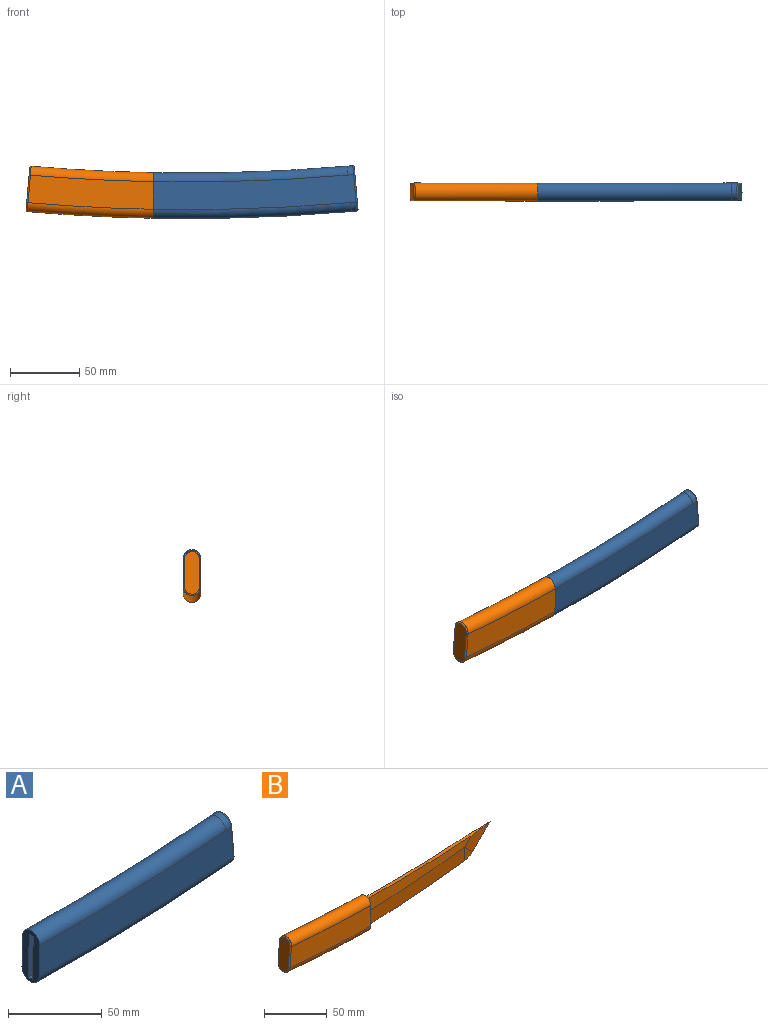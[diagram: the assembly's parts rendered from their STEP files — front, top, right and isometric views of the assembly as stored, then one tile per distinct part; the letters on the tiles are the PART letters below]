
ASSEMBLY  parts=2 mates=1
PART A: 17 faces, bbox 148.5x14.1x40.8 mm
  f0: cylinder r=1328mm len=140.41mm, axis (0,1,0), area 421.7mm2, adj f1,f3,f5,f8
  f1: plane 23.3x23.29mm, normal (-0.71,0,0.71), area 98.8mm2, adj f0,f2,f5,f8
  f2: cylinder r=1349.91mm len=117.63mm, axis (0,1,0), area 354.2mm2, adj f1,f3,f5,f8
  f3: plane 32.99x13mm, normal (-1,0,0.02), area 308.7mm2, adj f0,f2,f5,f6,f7,f8,f9,f11
  f4: plane 30.88x11mm, normal (1,0,0.09), area 315mm2, adj f13,f14,f15,f16
  f5: plane 140.94x32.77mm, normal (0,-1,0), area 3150.7mm2, adj f0,f1,f2,f3
  f6: plane 146.88x25.37mm, normal (0,1,0), area 2919.7mm2, adj f3,f9,f10,f11,f12,f14
  f7: plane 146.88x25.37mm, normal (0,-1,0), area 2919.7mm2, adj f3,f9,f10,f11,f12,f15
  f8: plane 140.94x32.77mm, normal (0,1,0), area 3150.7mm2, adj f0,f1,f2,f3
  f9: torus R=1351.5mm, axis (0,-1,0), area 2929.9mm2, adj f3,f6,f7,f10
  f10: cylinder r=6.5mm len=13mm, axis (1,0,0.09), area 81.7mm2, adj f6,f7,f9,f13
  f11: torus R=1331.5mm, axis (0,-1,0), area 2868.8mm2, adj f3,f6,f7,f12
  f12: cylinder r=6.5mm len=13mm, axis (-1,0,-0.09), area 81.7mm2, adj f6,f7,f11,f16
  f13: torus R=5.5mm, axis (1,0,0.09), area 30.3mm2, adj f4,f10,f14,f15
  f14: cylinder r=1mm len=20.01mm, axis (-0.09,0,1), area 31.4mm2, adj f4,f6,f13,f16
  f15: cylinder r=1mm len=20.01mm, axis (0.09,0,-1), area 31.4mm2, adj f4,f7,f13,f16
  f16: torus R=5.5mm, axis (1,0,0.09), area 30.3mm2, adj f4,f12,f14,f15
PART B: 19 faces, bbox 233.1x13x38.5 mm
  f0: plane 117.63x15.94mm, normal (0,1,0), area 1111.5mm2, adj f2,f4,f8,f12
  f1: plane 30.89x11mm, normal (-1,0,0.09), area 315mm2, adj f15,f16,f17,f18
  f2: plane 33x13mm, normal (1,0,-0.02), area 331.3mm2, adj f0,f3,f4,f5,f6,f7,f8,f13
  f3: plane 91.09x24.7mm, normal (0,-1,0), area 1803.5mm2, adj f2,f13,f14,f17
  f4: cylinder r=1328mm len=140.41mm, axis (0,1,0), area 387mm2, adj f0,f2,f5,f10,f12
  f5: plane 117.63x15.94mm, normal (0,-1,0), area 1111.5mm2, adj f2,f4,f7,f10
  f6: plane 91.09x24.7mm, normal (0,1,0), area 1803.5mm2, adj f2,f13,f14,f16
  f7: cone r=1334.91mm half-angle=84.3deg, axis (0,1,0), area 1685.6mm2, adj f2,f5,f8,f9
  f8: cone r=1349.91mm half-angle=84.3deg, axis (0,-1,0), area 1685.6mm2, adj f0,f2,f7,f11
  f9: cone r=15mm half-angle=84.3deg, axis (0,1,0), area 75.2mm2, adj f7,f10,f11
  f10: plane 30.26x19.65mm, normal (0.07,-1,-0.07), area 285.7mm2, adj f4,f5,f9,f12
  f11: cone r=15mm half-angle=84.3deg, axis (0,-1,0), area 75.2mm2, adj f8,f9,f12
  f12: plane 30.26x19.65mm, normal (0.07,1,-0.07), area 285.7mm2, adj f0,f4,f10,f11
  f13: torus R=1331.5mm, axis (0,-1,0), area 1821.8mm2, adj f2,f3,f6,f15
  f14: torus R=1351.5mm, axis (0,-1,0), area 1861mm2, adj f2,f3,f6,f18
  f15: bspline ~13x8.02mm, area 30.3mm2, adj f1,f13,f16,f17
  f16: cylinder r=1mm len=20.01mm, axis (-0.09,0,-1), area 31.4mm2, adj f1,f6,f15,f18
  f17: cylinder r=1mm len=20.01mm, axis (0.09,0,1), area 31.4mm2, adj f1,f3,f15,f18
  f18: bspline ~13x8.02mm, area 30.3mm2, adj f1,f14,f16,f17
PLACE A rot(axis=(0,1,0),0deg) t=(292.55,34.69,-102.62)mm fixed
PLACE B rot(axis=(0,-1,0),0deg) t=(-97.55,34.69,-15.68)mm
MATE revolute A.f0 <-> B.f4  axis (0,-1,0) through (17.45,34.69,1304.32)mm
